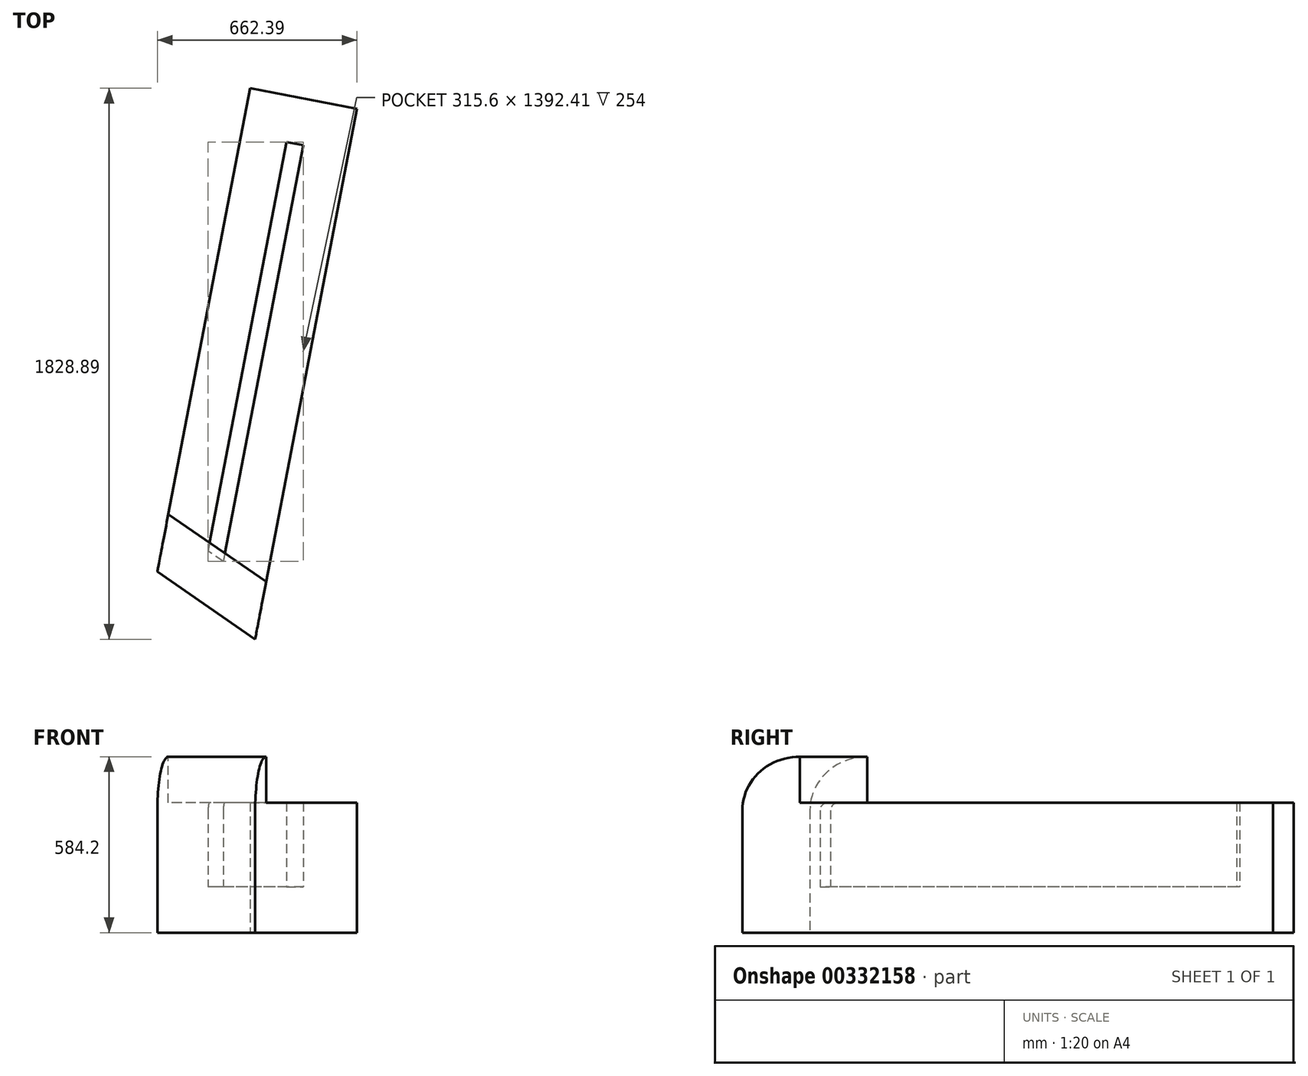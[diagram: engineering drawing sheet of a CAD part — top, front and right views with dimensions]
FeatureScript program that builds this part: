
annotation { "Feature Type Name" : "Feature", "Feature Type Description" : "" }
export const myFeature = defineFeature(function(context is Context, id is Id, definition is map)
    precondition{}
    {
        {
            var Q0;
            Q0=qCreatedBy(makeId("Top.planeOp"),FACE);
            var sketch = newSketch(context, id + "F0", { "sketchPlane" : qUnion([Q0])});
            skLineSegment(sketch, "E0", {"start": v(93.42, 617.1) * mm, "end": v(-167.03, -740.46) * mm});
            skLineSegment(sketch, "E1", {"start": v(93.42, 617.1) * mm, "end": v(148.57, 606.52) * mm});
            skLineSegment(sketch, "E2", {"start": v(148.57, 606.52) * mm, "end": v(-116.53, -775.31) * mm});
            skLineSegment(sketch, "E3", {"start": v(-116.53, -775.31) * mm, "end": v(-167.03, -740.46) * mm});
            skSolve(sketch);
        }
        {
            var Q0;
            Q0=makeQuery(id+"F0.imprint","IMPRINT",FACE,{"disambiguationData":[TD([[makeQuery(id+"F0.imprint","IMPRINT",EDGE,{"derivedFrom":sQuery(id+"F0.wireOp",EDGE,"E0")}),1.0]])]});
            extrude(context, id + "F1", {"entities" : qUnion([Q0]), "depth" : 254 * mm, "hasSecondDirection" : true, "secondDirectionOppositeDirection" : true, "secondDirectionDepth" : 25.4 * mm});
        }
        {
            var Q0;
            Q0=makeQuery(id+"F1.opExtrude","CAP_EDGE",EDGE,{"disambiguationData":[OSD([sQuery(id+"F0.wireOp",EDGE,"E3")])],"isStart":false});
            fillet(context, id + "F2", {"entities" : qUnion([Q0]), "radius" : 25.4 * mm, "tangentPropagation" : true, "allowEdgeOverflow" : false});
        }
        {
            var Q0;
            Q0=makeQuery(id+"F1.opExtrude","CAP_FACE",FACE,{"disambiguationData":[OSD([sQuery(id+"F0.wireOp",EDGE,"E0"),sQuery(id+"F0.wireOp",EDGE,"E1"),sQuery(id+"F0.wireOp",EDGE,"E2"),sQuery(id+"F0.wireOp",EDGE,"E3")])],"isStart":false});
            shell(context, id + "F3", {"entities" : qUnion([Q0]), "thickness" : 152.4 * mm, "oppositeDirection" : true});
        }
    });
